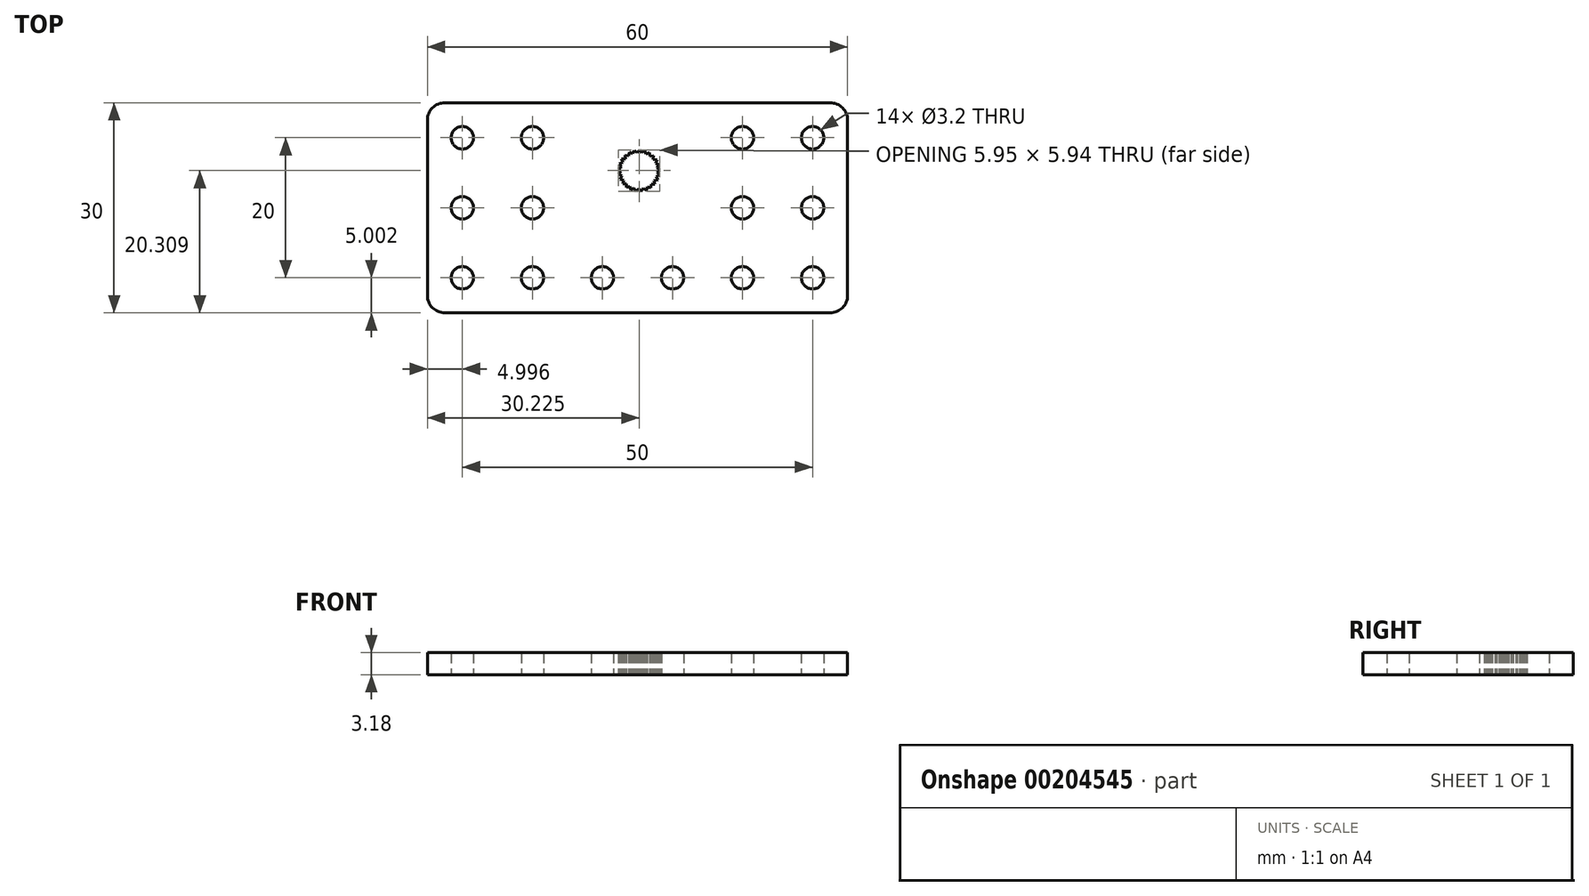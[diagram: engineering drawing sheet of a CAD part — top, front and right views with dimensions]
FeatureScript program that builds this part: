
annotation { "Feature Type Name" : "Feature", "Feature Type Description" : "" }
export const myFeature = defineFeature(function(context is Context, id is Id, definition is map)
    precondition{}
    {
        {
            var Q0;
            Q0=qCreatedBy(makeId("Top.planeOp"),FACE);
            var sketch = newSketch(context, id + "F0", { "sketchPlane" : qUnion([Q0])});
            skLineSegment(sketch, "E0.bottom", {"start": v(2.79, 0.24) * mm, "end": v(57.79, 0.24) * mm});
            skLineSegment(sketch, "E0.top", {"start": v(2.79, 30.24) * mm, "end": v(57.79, 30.24) * mm});
            skLineSegment(sketch, "E0.left", {"start": v(0.29, 2.74) * mm, "end": v(0.29, 27.74) * mm});
            skLineSegment(sketch, "E0.right", {"start": v(60.29, 2.74) * mm, "end": v(60.29, 27.74) * mm});
            skCircle(sketch, "E1", {"center": v(5.29, 25.24) * mm, "radius": 1.6 * mm});
            skCircle(sketch, "E2.0.1.0", {"center": v(5.29, 15.24) * mm, "radius": 1.6 * mm});
            skCircle(sketch, "E2.0.2.0", {"center": v(5.29, 5.24) * mm, "radius": 1.6 * mm});
            skCircle(sketch, "E2.1.0.0", {"center": v(15.29, 25.24) * mm, "radius": 1.6 * mm});
            skCircle(sketch, "E2.1.1.0", {"center": v(15.29, 15.24) * mm, "radius": 1.6 * mm});
            skCircle(sketch, "E2.1.2.0", {"center": v(15.29, 5.24) * mm, "radius": 1.6 * mm});
            skCircle(sketch, "E2.2.2.0", {"center": v(25.29, 5.24) * mm, "radius": 1.6 * mm});
            skCircle(sketch, "E2.3.2.0", {"center": v(35.29, 5.24) * mm, "radius": 1.6 * mm});
            skCircle(sketch, "E2.4.0.0", {"center": v(45.29, 25.24) * mm, "radius": 1.6 * mm});
            skCircle(sketch, "E2.4.1.0", {"center": v(45.29, 15.24) * mm, "radius": 1.6 * mm});
            skCircle(sketch, "E2.4.2.0", {"center": v(45.29, 5.24) * mm, "radius": 1.6 * mm});
            skCircle(sketch, "E2.5.0.0", {"center": v(55.29, 25.24) * mm, "radius": 1.6 * mm});
            skCircle(sketch, "E2.5.1.0", {"center": v(55.29, 15.24) * mm, "radius": 1.6 * mm});
            skCircle(sketch, "E2.5.2.0", {"center": v(55.29, 5.24) * mm, "radius": 1.6 * mm});
            skLineSegment(sketch, "E2.direction1", {"start": v(5.29, 25.24) * mm, "end": v(15.29, 25.24) * mm});
            skLineSegment(sketch, "E2.direction2", {"start": v(5.29, 25.24) * mm, "end": v(5.29, 15.24) * mm});
            skArc(sketch, "E3", {"start": v(2.79, 30.24) * mm, "mid": v(1.02, 29.5) * mm, "end": v(0.29, 27.74) * mm});
            skArc(sketch, "E4", {"start": v(60.29, 27.74) * mm, "mid": v(59.55, 29.5) * mm, "end": v(57.79, 30.24) * mm});
            skArc(sketch, "E5", {"start": v(57.79, 0.24) * mm, "mid": v(59.55, 0.97) * mm, "end": v(60.29, 2.74) * mm});
            skArc(sketch, "E6", {"start": v(0.29, 2.74) * mm, "mid": v(1.02, 0.97) * mm, "end": v(2.79, 0.24) * mm});
            skPoint(sketch, "E7.center", {"position": v(30.51, 20.54) * mm});
            skLineSegment(sketch, "E8", {"start": v(28.03, 22.2) * mm, "end": v(28.2, 21.7) * mm});
            skLineSegment(sketch, "E9", {"start": v(28.2, 21.7) * mm, "end": v(27.7, 21.52) * mm});
            skLineSegment(sketch, "E10.1.0", {"start": v(27.7, 21.52) * mm, "end": v(27.98, 21.08) * mm});
            skLineSegment(sketch, "E10.1.1", {"start": v(27.98, 21.08) * mm, "end": v(27.54, 20.8) * mm});
            skLineSegment(sketch, "E10.2.0", {"start": v(27.54, 20.8) * mm, "end": v(27.93, 20.44) * mm});
            skLineSegment(sketch, "E10.2.1", {"start": v(27.93, 20.44) * mm, "end": v(27.57, 20.05) * mm});
            skLineSegment(sketch, "E10.3.0", {"start": v(27.57, 20.05) * mm, "end": v(28.04, 19.8) * mm});
            skLineSegment(sketch, "E10.3.1", {"start": v(28.04, 19.8) * mm, "end": v(27.79, 19.33) * mm});
            skLineSegment(sketch, "E10.4.0", {"start": v(27.79, 19.33) * mm, "end": v(28.3, 19.2) * mm});
            skLineSegment(sketch, "E10.4.1", {"start": v(28.3, 19.2) * mm, "end": v(28.17, 18.7) * mm});
            skLineSegment(sketch, "E10.5.0", {"start": v(28.17, 18.7) * mm, "end": v(28.7, 18.7) * mm});
            skLineSegment(sketch, "E10.5.1", {"start": v(28.7, 18.7) * mm, "end": v(28.7, 18.17) * mm});
            skLineSegment(sketch, "E10.6.0", {"start": v(28.7, 18.17) * mm, "end": v(29.22, 18.3) * mm});
            skLineSegment(sketch, "E10.6.1", {"start": v(29.22, 18.3) * mm, "end": v(29.35, 17.8) * mm});
            skLineSegment(sketch, "E10.7.0", {"start": v(29.35, 17.8) * mm, "end": v(29.81, 18.05) * mm});
            skLineSegment(sketch, "E10.7.1", {"start": v(29.81, 18.05) * mm, "end": v(30.07, 17.6) * mm});
            skLineSegment(sketch, "E10.8.0", {"start": v(30.07, 17.6) * mm, "end": v(30.45, 17.96) * mm});
            skLineSegment(sketch, "E10.8.1", {"start": v(30.45, 17.96) * mm, "end": v(30.82, 17.58) * mm});
            skLineSegment(sketch, "E10.9.0", {"start": v(30.82, 17.58) * mm, "end": v(31.1, 18.03) * mm});
            skLineSegment(sketch, "E10.9.1", {"start": v(31.1, 18.03) * mm, "end": v(31.55, 17.75) * mm});
            skLineSegment(sketch, "E10.10.0", {"start": v(31.55, 17.75) * mm, "end": v(31.7, 18.25) * mm});
            skLineSegment(sketch, "E10.10.1", {"start": v(31.7, 18.25) * mm, "end": v(32.2, 18.1) * mm});
            skLineSegment(sketch, "E10.11.0", {"start": v(32.2, 18.1) * mm, "end": v(32.24, 18.62) * mm});
            skLineSegment(sketch, "E10.11.1", {"start": v(32.24, 18.62) * mm, "end": v(32.77, 18.6) * mm});
            skLineSegment(sketch, "E10.12.0", {"start": v(32.77, 18.6) * mm, "end": v(32.66, 19.1) * mm});
            skLineSegment(sketch, "E10.12.1", {"start": v(32.66, 19.1) * mm, "end": v(33.18, 19.21) * mm});
            skLineSegment(sketch, "E10.13.0", {"start": v(33.18, 19.21) * mm, "end": v(32.95, 19.69) * mm});
            skLineSegment(sketch, "E10.13.1", {"start": v(32.95, 19.69) * mm, "end": v(33.43, 19.92) * mm});
            skLineSegment(sketch, "E10.14.0", {"start": v(33.43, 19.92) * mm, "end": v(33.09, 20.32) * mm});
            skLineSegment(sketch, "E10.14.1", {"start": v(33.09, 20.32) * mm, "end": v(33.49, 20.66) * mm});
            skLineSegment(sketch, "E10.15.0", {"start": v(33.49, 20.66) * mm, "end": v(33.06, 20.97) * mm});
            skLineSegment(sketch, "E10.15.1", {"start": v(33.06, 20.97) * mm, "end": v(33.37, 21.4) * mm});
            skLineSegment(sketch, "E10.16.0", {"start": v(33.37, 21.4) * mm, "end": v(32.87, 21.6) * mm});
            skLineSegment(sketch, "E10.16.1", {"start": v(32.87, 21.6) * mm, "end": v(33.06, 22.08) * mm});
            skLineSegment(sketch, "E10.17.0", {"start": v(33.06, 22.08) * mm, "end": v(32.54, 22.14) * mm});
            skLineSegment(sketch, "E10.17.1", {"start": v(32.54, 22.14) * mm, "end": v(32.6, 22.67) * mm});
            skLineSegment(sketch, "E10.18.0", {"start": v(32.6, 22.67) * mm, "end": v(32.07, 22.6) * mm});
            skLineSegment(sketch, "E10.18.1", {"start": v(32.07, 22.6) * mm, "end": v(32, 23.12) * mm});
            skLineSegment(sketch, "E10.19.0", {"start": v(32, 23.12) * mm, "end": v(31.51, 22.92) * mm});
            skLineSegment(sketch, "E10.19.1", {"start": v(31.51, 22.92) * mm, "end": v(31.31, 23.41) * mm});
            skLineSegment(sketch, "E10.20.0", {"start": v(31.31, 23.41) * mm, "end": v(30.9, 23.1) * mm});
            skLineSegment(sketch, "E10.20.1", {"start": v(30.9, 23.1) * mm, "end": v(30.58, 23.52) * mm});
            skLineSegment(sketch, "E10.21.0", {"start": v(30.58, 23.52) * mm, "end": v(30.24, 23.11) * mm});
            skLineSegment(sketch, "E10.21.1", {"start": v(30.24, 23.11) * mm, "end": v(29.83, 23.44) * mm});
            skLineSegment(sketch, "E10.22.0", {"start": v(29.83, 23.44) * mm, "end": v(29.61, 22.96) * mm});
            skLineSegment(sketch, "E10.22.1", {"start": v(29.61, 22.96) * mm, "end": v(29.13, 23.18) * mm});
            skLineSegment(sketch, "E10.23.0", {"start": v(29.13, 23.18) * mm, "end": v(29.04, 22.66) * mm});
            skLineSegment(sketch, "E10.23.1", {"start": v(29.04, 22.66) * mm, "end": v(28.52, 22.76) * mm});
            skLineSegment(sketch, "E10.24.0", {"start": v(28.52, 22.76) * mm, "end": v(28.56, 22.23) * mm});
            skLineSegment(sketch, "E10.24.1", {"start": v(28.56, 22.23) * mm, "end": v(28.03, 22.2) * mm});
            skSolve(sketch);
        }
        {
            var Q0;
            Q0=makeQuery(id+"F0.imprint","IMPRINT",FACE,{"disambiguationData":[TD([[makeQuery(id+"F0.imprint","IMPRINT",EDGE,{"derivedFrom":sQuery(id+"F0.wireOp",EDGE,"E0.bottom")}),1.0]])]});
            extrude(context, id + "F1", {"entities" : qUnion([Q0]), "depth" : 3.17 * mm});
        }
    });
